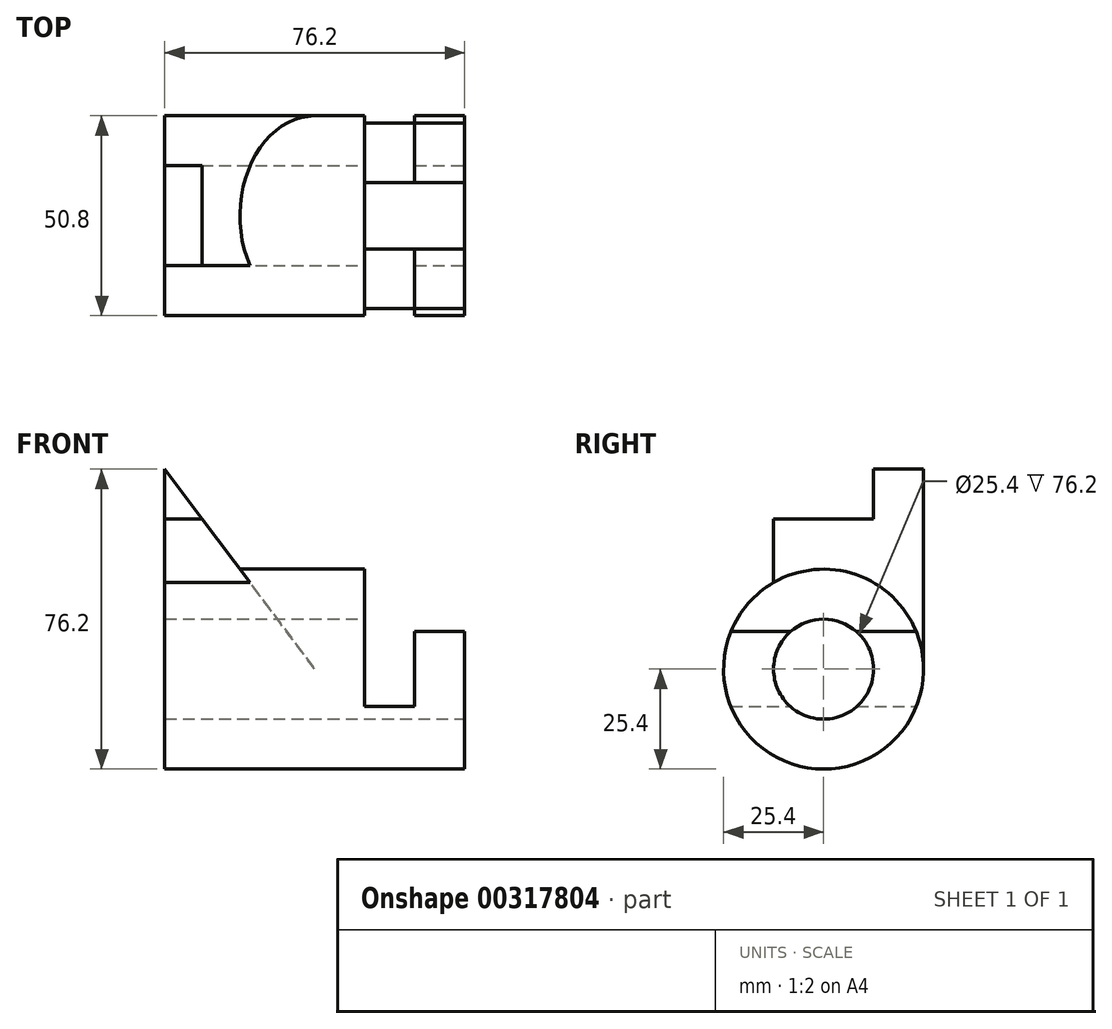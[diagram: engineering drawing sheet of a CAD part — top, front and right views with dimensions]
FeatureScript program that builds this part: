
annotation { "Feature Type Name" : "Feature", "Feature Type Description" : "" }
export const myFeature = defineFeature(function(context is Context, id is Id, definition is map)
    precondition{}
    {
        {
            var Q0;
            Q0=qCreatedBy(makeId("Front.planeOp"),FACE);
            var sketch = newSketch(context, id + "F0", { "sketchPlane" : qUnion([Q0])});
            skLineSegment(sketch, "E0", {"start": v(0, 0) * mm, "end": v(0, 50.8) * mm});
            skLineSegment(sketch, "E1", {"start": v(0, 50.8) * mm, "end": v(38.1, 0) * mm});
            skLineSegment(sketch, "E2", {"start": v(38.1, 0) * mm, "end": v(0, 0) * mm});
            skSolve(sketch);
        }
        {
            var Q0;
            Q0 = qSketchRegion(id + "F0", true);
            extrude(context, id + "F1", {"entities" : qUnion([Q0]), "depth" : 38.1 * mm});
        }
        {
            var Q0;
            Q0=qCreatedBy(makeId("Right.planeOp"),FACE);
            var sketch = newSketch(context, id + "F2", { "sketchPlane" : qUnion([Q0])});
            skCircle(sketch, "E3", {"center": v(-25.4, 0) * mm, "radius": 25.4 * mm});
            skSolve(sketch);
        }
        {
            var Q0;
            Q0 = qSketchRegion(id + "F2", true);
            extrude(context, id + "F3", {"entities" : qUnion([Q0]), "operationType" : NewBodyOperationType.ADD, "depth" : 76.2 * mm});
        }
        {
            var Q0;
            Q0=makeQuery(id+"F3.opExtrude","CAP_FACE",FACE,{"disambiguationData":[OSD([sQuery(id+"F2.wireOp",EDGE,"E3")])],"isStart":false});
            var sketch = newSketch(context, id + "F4", { "sketchPlane" : qUnion([Q0])});
            skCircle(sketch, "E4", {"center": v(-25.4, 0) * mm, "radius": 12.7 * mm});
            skSolve(sketch);
        }
        {
            var Q0;
            Q0=makeQuery(id+"F4.imprint","IMPRINT",FACE,{"disambiguationData":[TD([[makeQuery(id+"F4.imprint","IMPRINT",EDGE,{"derivedFrom":sQuery(id+"F4.wireOp",EDGE,"E4")}),1.0]])]});
            extrude(context, id + "F5", {"entities" : qUnion([Q0]), "operationType" : NewBodyOperationType.REMOVE, "endBound" : BoundingType.THROUGH_ALL, "oppositeDirection" : true, "depth" : 25.4 * mm});
        }
        {
            var Q0;
            Q0=qCreatedBy(makeId("Front.planeOp"),FACE);
            var sketch = newSketch(context, id + "F6", { "sketchPlane" : qUnion([Q0])});
            skLineSegment(sketch, "E5", {"start": v(50.8, 25.4) * mm, "end": v(50.8, -9.52) * mm});
            skLineSegment(sketch, "E6", {"start": v(50.8, -9.52) * mm, "end": v(63.5, -9.52) * mm});
            skLineSegment(sketch, "E7", {"start": v(63.5, -9.52) * mm, "end": v(63.5, 9.53) * mm});
            skLineSegment(sketch, "E8", {"start": v(63.5, 9.53) * mm, "end": v(76.2, 9.53) * mm});
            skLineSegment(sketch, "E9", {"start": v(76.2, 9.53) * mm, "end": v(76.2, 25.4) * mm});
            skLineSegment(sketch, "E10", {"start": v(76.2, 25.4) * mm, "end": v(50.8, 25.4) * mm});
            skSolve(sketch);
        }
        {
            var Q0;
            Q0 = qSketchRegion(id + "F6", true);
            extrude(context, id + "F7", {"entities" : qUnion([Q0]), "operationType" : NewBodyOperationType.REMOVE, "endBound" : BoundingType.THROUGH_ALL, "depth" : 25.4 * mm});
        }
        {
            var Q0;
            Q0=qCreatedBy(makeId("Right.planeOp"),FACE);
            var sketch = newSketch(context, id + "F8", { "sketchPlane" : qUnion([Q0])});
            skLineSegment(sketch, "E11", {"start": v(-38.1, 38.1) * mm, "end": v(-12.7, 38.1) * mm});
            skLineSegment(sketch, "E12", {"start": v(-12.7, 38.1) * mm, "end": v(-12.7, 50.8) * mm});
            skLineSegment(sketch, "E13", {"start": v(-12.7, 50.8) * mm, "end": v(-38.1, 50.8) * mm});
            skLineSegment(sketch, "E14", {"start": v(-38.1, 50.8) * mm, "end": v(-38.1, 38.1) * mm});
            skSolve(sketch);
        }
        {
            var Q0;
            Q0 = qSketchRegion(id + "F8", true);
            extrude(context, id + "F9", {"entities" : qUnion([Q0]), "operationType" : NewBodyOperationType.REMOVE, "depth" : 25.4 * mm});
        }
    });
